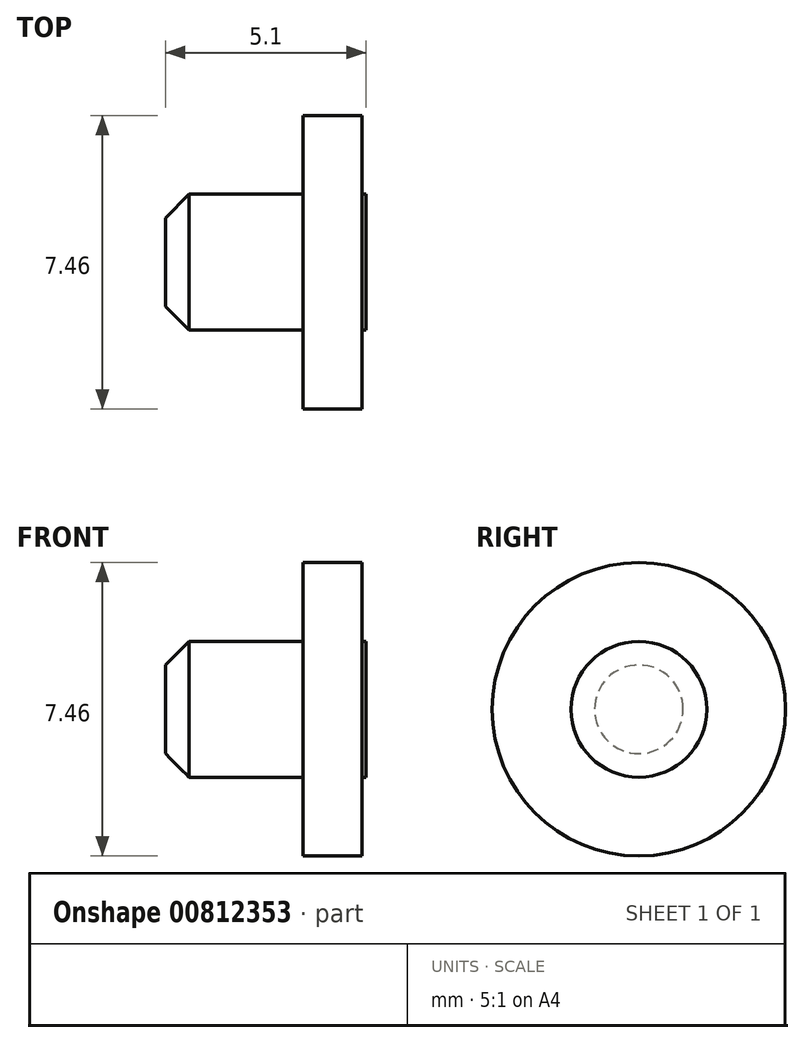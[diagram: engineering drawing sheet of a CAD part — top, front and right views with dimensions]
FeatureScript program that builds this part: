
annotation { "Feature Type Name" : "Feature", "Feature Type Description" : "" }
export const myFeature = defineFeature(function(context is Context, id is Id, definition is map)
    precondition{}
    {
        {
            var Q0;
            Q0=qCreatedBy(makeId("Right.planeOp"),FACE);
            var sketch = newSketch(context, id + "F0", { "sketchPlane" : qUnion([Q0])});
            skCircle(sketch, "E0", {"center": v(0, 0) * mm, "radius": 3.73 * mm});
            skSolve(sketch);
        }
        {
            var Q0;
            Q0=makeQuery(id+"F0.imprint","IMPRINT",FACE,{"disambiguationData":[TD([[makeQuery(id+"F0.imprint","IMPRINT",EDGE,{"derivedFrom":sQuery(id+"F0.wireOp",EDGE,"E0")}),1.0]])]});
            extrude(context, id + "F1", {"entities" : qUnion([Q0]), "depth" : 1.5 * mm, "offsetDistance" : 25 * mm});
        }
        {
            var Q0;
            Q0=qCreatedBy(makeId("Right.planeOp"),FACE);
            var sketch = newSketch(context, id + "F2", { "sketchPlane" : qUnion([Q0])});
            skCircle(sketch, "E1", {"center": v(0, 0) * mm, "radius": 1.72 * mm});
            skSolve(sketch);
        }
        {
            var Q0;
            Q0 = qSketchRegion(id + "F2", true);
            extrude(context, id + "F3", {"entities" : qUnion([Q0]), "operationType" : NewBodyOperationType.ADD, "oppositeDirection" : true, "depth" : 3.5 * mm, "offsetDistance" : 25 * mm});
        }
        {
            var Q0;
            Q0=qCreatedBy(makeId("Right.planeOp"),FACE);
            var sketch = newSketch(context, id + "F4", { "sketchPlane" : qUnion([Q0])});
            skCircle(sketch, "E2", {"center": v(0, 0) * mm, "radius": 1.72 * mm});
            skSolve(sketch);
        }
        {
            var Q0;
            Q0 = qSketchRegion(id + "F4", true);
            extrude(context, id + "F5", {"entities" : qUnion([Q0]), "operationType" : NewBodyOperationType.ADD, "depth" : 1.6 * mm, "offsetDistance" : 25 * mm});
        }
        {
            var Q0;
            Q0=makeQuery(id+"F3.opExtrude","CAP_EDGE",EDGE,{"disambiguationData":[OSD([sQuery(id+"F2.wireOp",EDGE,"E1")])],"isStart":false});
            chamfer(context, id + "F6", {"entities" : qUnion([Q0]), "width" : 0.6 * mm, "tangentPropagation" : true});
        }
    });
